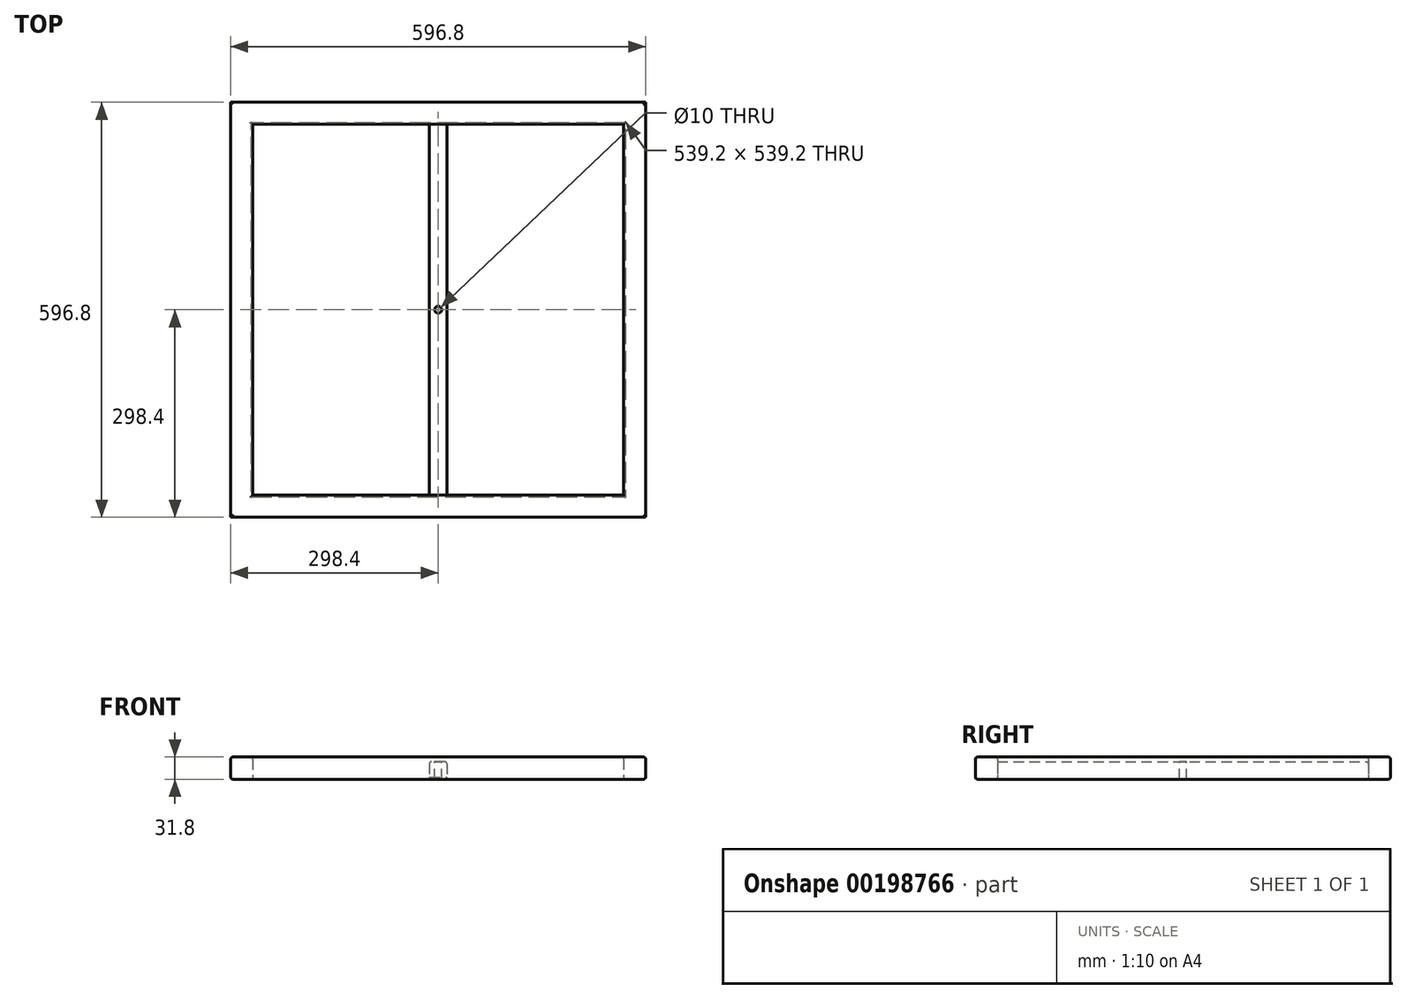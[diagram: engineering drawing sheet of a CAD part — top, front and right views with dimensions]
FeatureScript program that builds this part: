
annotation { "Feature Type Name" : "Feature", "Feature Type Description" : "" }
export const myFeature = defineFeature(function(context is Context, id is Id, definition is map)
    precondition{}
    {
        {
            var Q0;
            Q0=qCreatedBy(makeId("Top.planeOp"),FACE);
            var sketch = newSketch(context, id + "F0", { "sketchPlane" : qUnion([Q0])});
            skLineSegment(sketch, "E0.bottom", {"start": v(-298.4, 298.4) * mm, "end": v(298.4, 298.4) * mm});
            skLineSegment(sketch, "E0.top", {"start": v(-298.4, -298.4) * mm, "end": v(298.4, -298.4) * mm});
            skLineSegment(sketch, "E0.left", {"start": v(-298.4, 298.4) * mm, "end": v(-298.4, -298.4) * mm});
            skLineSegment(sketch, "E0.right", {"start": v(298.4, 298.4) * mm, "end": v(298.4, -298.4) * mm});
            skPoint(sketch, "E0.middle", {"position": v(0, 0) * mm});
            skLineSegment(sketch, "E1.0", {"start": v(-266.6, -266.6) * mm, "end": v(266.6, -266.6) * mm});
            skLineSegment(sketch, "E1.1", {"start": v(-266.6, 266.6) * mm, "end": v(-266.6, -266.6) * mm});
            skLineSegment(sketch, "E1.2", {"start": v(-266.6, 266.6) * mm, "end": v(266.6, 266.6) * mm});
            skLineSegment(sketch, "E1.3", {"start": v(266.6, 266.6) * mm, "end": v(266.6, -266.6) * mm});
            skSolve(sketch);
        }
        {
            var Q0;
            Q0 = qSketchRegion(id + "F0", true);
            extrude(context, id + "F1", {"entities" : qUnion([Q0]), "depth" : 31.8 * mm, "symmetric" : true});
        }
        {
            var Q0;
            Q0=makeQuery(id+"F1.opExtrude","CAP_EDGE",EDGE,{"disambiguationData":[OSD([sQuery(id+"F0.wireOp",EDGE,"E1.3")])],"isStart":false});
            var Q1;
            Q1=makeQuery(id+"F1.opExtrude","CAP_EDGE",EDGE,{"disambiguationData":[OSD([sQuery(id+"F0.wireOp",EDGE,"E1.2")])],"isStart":false});
            var Q2;
            Q2=makeQuery(id+"F1.opExtrude","CAP_EDGE",EDGE,{"disambiguationData":[OSD([sQuery(id+"F0.wireOp",EDGE,"E1.3")])],"isStart":true});
            var Q3;
            Q3=makeQuery(id+"F1.opExtrude","CAP_EDGE",EDGE,{"disambiguationData":[OSD([sQuery(id+"F0.wireOp",EDGE,"E1.2")])],"isStart":true});
            var Q4;
            Q4=makeQuery(id+"F1.opExtrude","CAP_EDGE",EDGE,{"disambiguationData":[OSD([sQuery(id+"F0.wireOp",EDGE,"E1.0")])],"isStart":true});
            var Q5;
            Q5=makeQuery(id+"F1.opExtrude","CAP_EDGE",EDGE,{"disambiguationData":[OSD([sQuery(id+"F0.wireOp",EDGE,"E1.0")])],"isStart":false});
            var Q6;
            Q6=makeQuery(id+"F1.opExtrude","CAP_EDGE",EDGE,{"disambiguationData":[OSD([sQuery(id+"F0.wireOp",EDGE,"E1.1")])],"isStart":false});
            var Q7;
            Q7=makeQuery(id+"F1.opExtrude","CAP_EDGE",EDGE,{"disambiguationData":[OSD([sQuery(id+"F0.wireOp",EDGE,"E1.1")])],"isStart":true});
            var Q8;
            Q8=makeQuery(id+"F1.opExtrude","CAP_EDGE",EDGE,{"disambiguationData":[OSD([sQuery(id+"F0.wireOp",EDGE,"E0.right")])],"isStart":false});
            var Q9;
            Q9=makeQuery(id+"F1.opExtrude","CAP_EDGE",EDGE,{"disambiguationData":[OSD([sQuery(id+"F0.wireOp",EDGE,"E0.right")])],"isStart":true});
            var Q10;
            Q10=makeQuery(id+"F1.opExtrude","CAP_EDGE",EDGE,{"disambiguationData":[OSD([sQuery(id+"F0.wireOp",EDGE,"E0.bottom")])],"isStart":false});
            var Q11;
            Q11=makeQuery(id+"F1.opExtrude","CAP_EDGE",EDGE,{"disambiguationData":[OSD([sQuery(id+"F0.wireOp",EDGE,"E0.bottom")])],"isStart":true});
            var Q12;
            Q12=makeQuery(id+"F1.opExtrude","CAP_EDGE",EDGE,{"disambiguationData":[OSD([sQuery(id+"F0.wireOp",EDGE,"E0.top")])],"isStart":false});
            var Q13;
            Q13=makeQuery(id+"F1.opExtrude","CAP_EDGE",EDGE,{"disambiguationData":[OSD([sQuery(id+"F0.wireOp",EDGE,"E0.top")])],"isStart":true});
            var Q14;
            Q14=makeQuery(id+"F1.opExtrude","CAP_EDGE",EDGE,{"disambiguationData":[OSD([sQuery(id+"F0.wireOp",EDGE,"E0.left")])],"isStart":true});
            var Q15;
            Q15=makeQuery(id+"F1.opExtrude","CAP_EDGE",EDGE,{"disambiguationData":[OSD([sQuery(id+"F0.wireOp",EDGE,"E0.left")])],"isStart":false});
            fillet(context, id + "F2", {"entities" : qUnion([Q0, Q1, Q2, Q3, Q4, Q5, Q6, Q7, Q8, Q9, Q10, Q11, Q12, Q13, Q14, Q15]), "radius" : 3 * mm, "tangentPropagation" : true, "allowEdgeOverflow" : false});
        }
        {
            var Q0;
            Q0=makeQuery(id+"F1.opExtrude","CAP_FACE",FACE,{"disambiguationData":[OSD([sQuery(id+"F0.wireOp",EDGE,"E0.bottom"),sQuery(id+"F0.wireOp",EDGE,"E0.top"),sQuery(id+"F0.wireOp",EDGE,"E0.left"),sQuery(id+"F0.wireOp",EDGE,"E0.right"),sQuery(id+"F0.wireOp",EDGE,"E1.0"),sQuery(id+"F0.wireOp",EDGE,"E1.1"),sQuery(id+"F0.wireOp",EDGE,"E1.2"),sQuery(id+"F0.wireOp",EDGE,"E1.3")])],"isStart":true});
            var sketch = newSketch(context, id + "F3", { "sketchPlane" : qUnion([Q0])});
            skLineSegment(sketch, "E2.bottom", {"start": v(12.5, -266.6) * mm, "end": v(-12.5, -266.6) * mm});
            skLineSegment(sketch, "E2.top", {"start": v(12.5, 266.6) * mm, "end": v(-12.5, 266.6) * mm});
            skLineSegment(sketch, "E2.left", {"start": v(12.5, 266.6) * mm, "end": v(12.5, -266.6) * mm});
            skLineSegment(sketch, "E2.right", {"start": v(-12.5, 266.6) * mm, "end": v(-12.5, -266.6) * mm});
            skPoint(sketch, "E2.middle", {"position": v(0, 0) * mm});
            skSolve(sketch);
        }
        {
            var Q0;
            Q0 = qSketchRegion(id + "F3", true);
            extrude(context, id + "F4", {"entities" : qUnion([Q0]), "operationType" : NewBodyOperationType.ADD, "oppositeDirection" : true, "depth" : 25 * mm});
        }
        {
            var Q0;
            Q0=makeQuery(id+"F4.opExtrude","CAP_EDGE",EDGE,{"disambiguationData":[OSD([sQuery(id+"F3.wireOp",EDGE,"E2.right")])],"isStart":false});
            var Q1;
            Q1=makeQuery(id+"F4.opExtrude","CAP_EDGE",EDGE,{"disambiguationData":[OSD([sQuery(id+"F3.wireOp",EDGE,"E2.left")])],"isStart":false});
            var Q2;
            Q2=makeQuery(id+"F4.opExtrude","CAP_EDGE",EDGE,{"disambiguationData":[OSD([sQuery(id+"F3.wireOp",EDGE,"E2.left")])],"isStart":true});
            var Q3;
            Q3=makeQuery(id+"F4.opExtrude","CAP_EDGE",EDGE,{"disambiguationData":[OSD([sQuery(id+"F3.wireOp",EDGE,"E2.right")])],"isStart":true});
            fillet(context, id + "F5", {"entities" : qUnion([Q0, Q1, Q2, Q3]), "radius" : 3 * mm, "tangentPropagation" : true, "allowEdgeOverflow" : false});
        }
        {
            var Q0;
            Q0=qCreatedBy(makeId("Top.planeOp"),FACE);
            var sketch = newSketch(context, id + "F6", { "sketchPlane" : qUnion([Q0])});
            skCircle(sketch, "E3", {"center": v(0, 0) * mm, "radius": 5 * mm});
            skSolve(sketch);
        }
        {
            var Q0;
            Q0 = qSketchRegion(id + "F6", true);
            extrude(context, id + "F7", {"entities" : qUnion([Q0]), "operationType" : NewBodyOperationType.REMOVE, "endBound" : BoundingType.THROUGH_ALL, "oppositeDirection" : true, "depth" : 25 * mm, "hasSecondDirection" : true, "secondDirectionBound" : BoundingType.THROUGH_ALL, "secondDirectionOppositeDirection" : false, "secondDirectionDepth" : 25 * mm});
        }
    });
